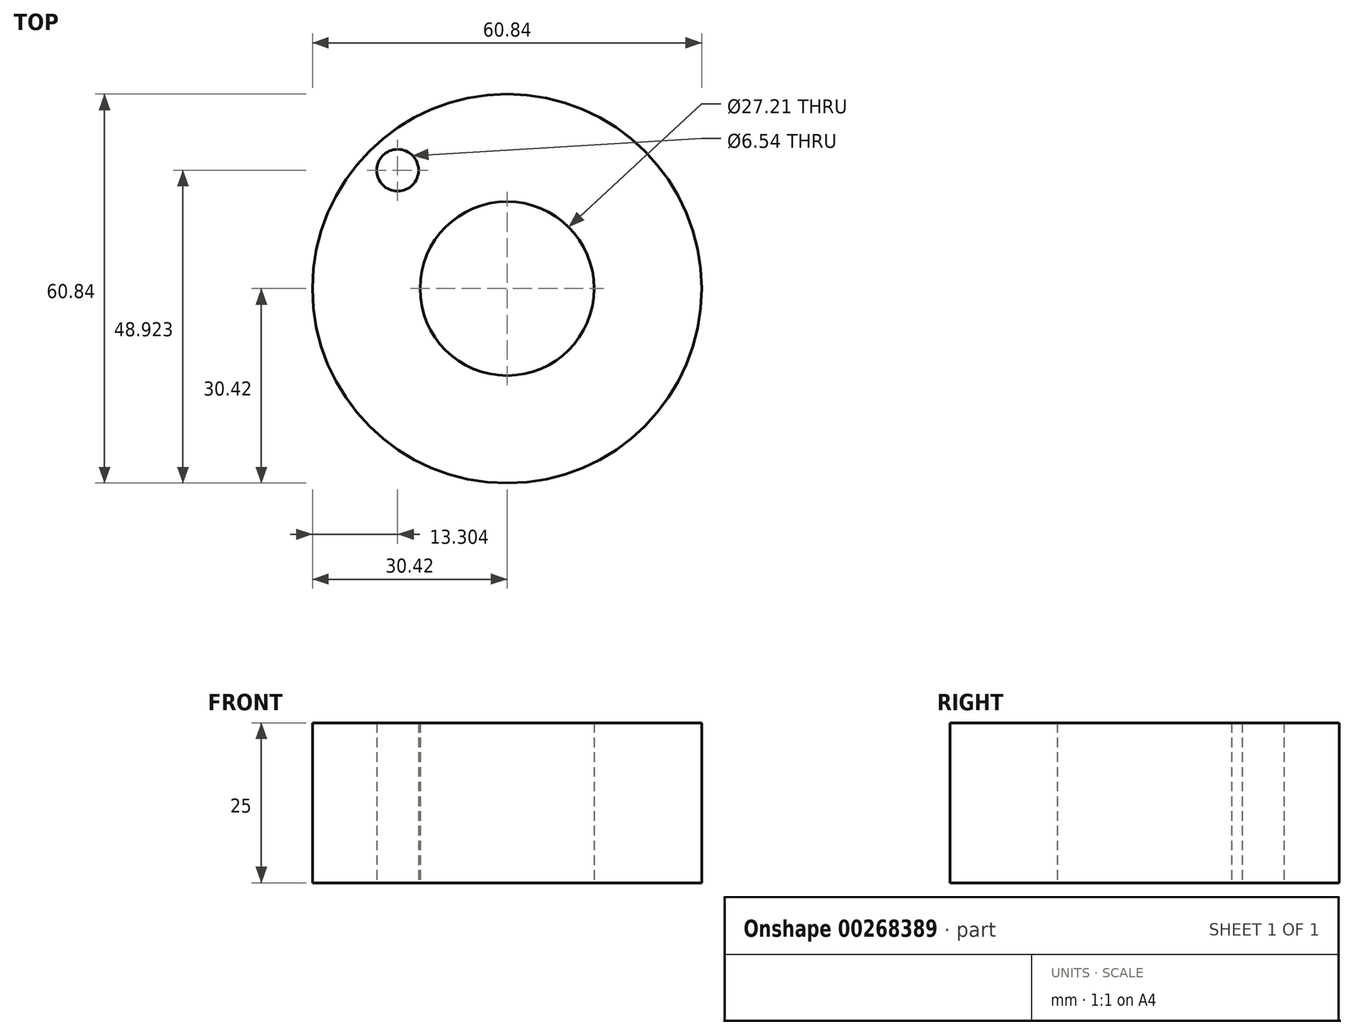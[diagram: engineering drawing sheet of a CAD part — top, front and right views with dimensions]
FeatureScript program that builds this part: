
annotation { "Feature Type Name" : "Feature", "Feature Type Description" : "" }
export const myFeature = defineFeature(function(context is Context, id is Id, definition is map)
    precondition{}
    {
        {
            var Q0;
            Q0=qCreatedBy(makeId("Top.planeOp"),FACE);
            var sketch = newSketch(context, id + "F0", { "sketchPlane" : qUnion([Q0])});
            skCircle(sketch, "E0", {"center": v(0, 0) * mm, "radius": 30.42 * mm});
            skCircle(sketch, "E1", {"center": v(0, 0) * mm, "radius": 13.6 * mm});
            skCircle(sketch, "E2", {"center": v(-17.12, 18.5) * mm, "radius": 3.27 * mm});
            skSolve(sketch);
        }
        {
            var Q0;
            Q0=makeQuery(id+"F0.imprint","IMPRINT",FACE,{"disambiguationData":[TD([[makeQuery(id+"F0.imprint","IMPRINT",EDGE,{"derivedFrom":sQuery(id+"F0.wireOp",EDGE,"E0")}),1.0]])]});
            extrude(context, id + "F1", {"entities" : qUnion([Q0]), "depth" : 25 * mm});
        }
    });
